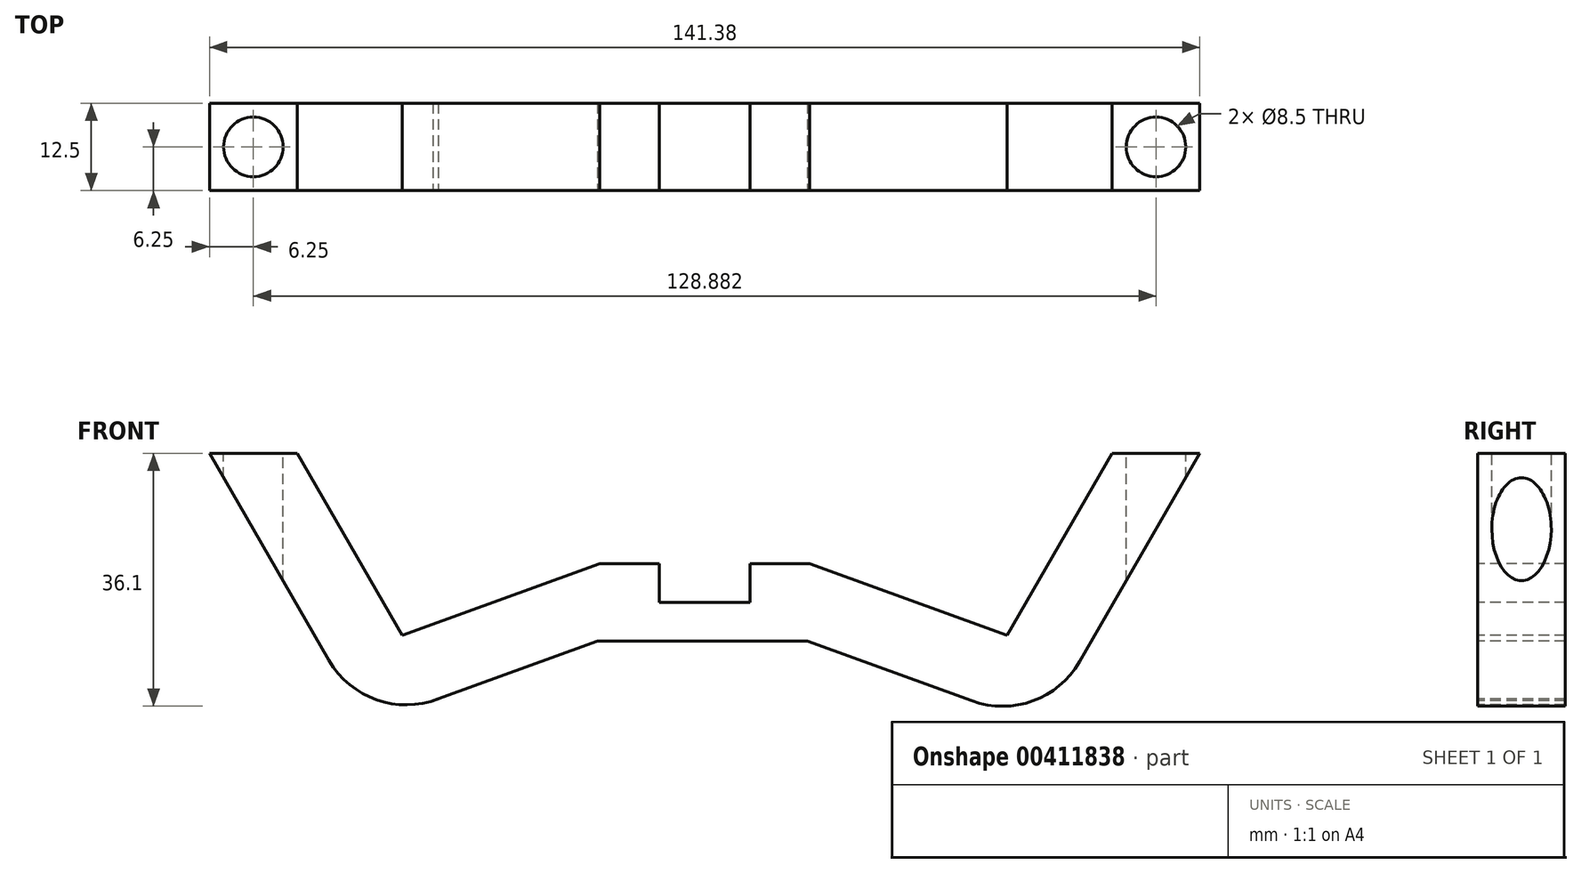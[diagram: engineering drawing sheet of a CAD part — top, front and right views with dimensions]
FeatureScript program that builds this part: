
annotation { "Feature Type Name" : "Feature", "Feature Type Description" : "" }
export const myFeature = defineFeature(function(context is Context, id is Id, definition is map)
    precondition{}
    {
        {
            var Q0;
            Q0=qCreatedBy(makeId("Front.planeOp"),FACE);
            var sketch = newSketch(context, id + "F0", { "sketchPlane" : qUnion([Q0])});
            skLineSegment(sketch, "E0", {"start": v(-35.95, 26.78) * mm, "end": v(-48.45, 26.78) * mm});
            skLineSegment(sketch, "E1", {"start": v(-48.45, 26.78) * mm, "end": v(-63.45, 0.8) * mm});
            skLineSegment(sketch, "E2", {"start": v(-35.95, 26.78) * mm, "end": v(-53.12, -2.97) * mm});
            skLineSegment(sketch, "E3", {"start": v(-63.45, 0.8) * mm, "end": v(-91.64, 11.06) * mm});
            skLineSegment(sketch, "E4", {"start": v(-68.46, -8.55) * mm, "end": v(-91.95, 0) * mm});
            skPoint(sketch, "E5.visualSharp", {"position": v(-58.45, -12.2) * mm});
            skArc(sketch, "E5.filletArc", {"start": v(-68.46, -8.55) * mm, "mid": v(-59.77, -8.55) * mm, "end": v(-53.12, -2.97) * mm});
            skLineSegment(sketch, "E6", {"start": v(-91.64, 11.06) * mm, "end": v(-121.64, 11.06) * mm});
            skLineSegment(sketch, "E7", {"start": v(-91.95, 0) * mm, "end": v(-121.95, 0) * mm});
            skPoint(sketch, "E8", {"position": v(-100.14, 11.06) * mm});
            skPoint(sketch, "E9", {"position": v(-113.14, 11.06) * mm});
            skLineSegment(sketch, "E10", {"start": v(-113.14, 11.06) * mm, "end": v(-113.14, 0) * mm});
            skLineSegment(sketch, "E11", {"start": v(-100.14, 11.06) * mm, "end": v(-100.14, 0) * mm});
            skPoint(sketch, "E12", {"position": v(-113.14, 5.53) * mm});
            skPoint(sketch, "E13", {"position": v(-100.14, 5.53) * mm});
            skLineSegment(sketch, "E14", {"start": v(-113.14, 5.53) * mm, "end": v(-100.14, 5.53) * mm});
            skLineSegment(sketch, "E15", {"start": v(-121.64, 11.06) * mm, "end": v(-149.83, 0.8) * mm});
            skLineSegment(sketch, "E16", {"start": v(-121.95, 0) * mm, "end": v(-145.45, -8.55) * mm});
            skLineSegment(sketch, "E17", {"start": v(-149.83, 0.8) * mm, "end": v(-164.83, 26.78) * mm});
            skLineSegment(sketch, "E18", {"start": v(-164.83, 26.78) * mm, "end": v(-177.33, 26.78) * mm});
            skLineSegment(sketch, "E19", {"start": v(-177.33, 26.78) * mm, "end": v(-160.28, -2.76) * mm});
            skLineSegment(sketch, "E20", {"start": v(-144.68, -8.25) * mm, "end": v(-145.45, -8.55) * mm});
            skPoint(sketch, "E21.visualSharp", {"position": v(-154.83, -12.2) * mm});
            skArc(sketch, "E21.filletArc", {"start": v(-160.28, -2.76) * mm, "mid": v(-153.5, -8.4) * mm, "end": v(-144.68, -8.25) * mm});
            skSolve(sketch);
        }
        {
            var Q0;
            {var subQ1=sQuery(id+"F0.wireOp",EDGE,"E15");Q0=makeQuery(id+"F0.imprint","IMPRINT",FACE,{"disambiguationData":[TD([[makeQuery(id+"F0.imprint","IMPRINT",EDGE,{"derivedFrom":subQ1}),1.0]])]});}
            var Q1;
            {var subQ5=sQuery(id+"F0.wireOp",EDGE,"E14");Q1=makeQuery(id+"F0.imprint","IMPRINT",FACE,{"disambiguationData":[TD([[makeQuery(id+"F0.imprint","IMPRINT",EDGE,{"derivedFrom":subQ5}),1.0]])]});}
            var Q2;
            {var subQ5=sQuery(id+"F0.wireOp",EDGE,"E14");Q2=makeQuery(id+"F0.imprint","IMPRINT",FACE,{"disambiguationData":[TD([[makeQuery(id+"F0.imprint","IMPRINT",EDGE,{"derivedFrom":subQ5}),-1.0]])]});}
            var Q3;
            Q3=makeQuery(id+"F0.imprint","IMPRINT",FACE,{"disambiguationData":[TD([[makeQuery(id+"F0.imprint","IMPRINT",EDGE,{"derivedFrom":sQuery(id+"F0.wireOp",EDGE,"E0")}),1.0]])]});
            extrude(context, id + "F1", {"entities" : qUnion([Q0, Q1, Q2, Q3]), "oppositeDirection" : true, "depth" : 12.5 * mm, "offsetDistance" : 25.4 * mm});
        }
        {
            var Q0;
            Q0=makeQuery(id+"F1.opExtrude","SWEPT_FACE",FACE,{"disambiguationData":[OSD([sQuery(id+"F0.wireOp",EDGE,"E0")])]});
            var sketch = newSketch(context, id + "F2", { "sketchPlane" : qUnion([Q0])});
            skCircle(sketch, "E22", {"center": v(-42.2, 6.25) * mm, "radius": 4.25 * mm});
            skPoint(sketch, "E22.centerSnap0", {"position": v(-42.2, 12.5) * mm});
            skPoint(sketch, "E22.centerSnap1", {"position": v(-35.95, 6.25) * mm});
            skSolve(sketch);
        }
        {
            var Q0;
            Q0=makeQuery(id+"F1.opExtrude","SWEPT_FACE",FACE,{"disambiguationData":[OSD([sQuery(id+"F0.wireOp",EDGE,"E18")])]});
            var sketch = newSketch(context, id + "F3", { "sketchPlane" : qUnion([Q0])});
            skCircle(sketch, "E23", {"center": v(-171.08, 6.25) * mm, "radius": 4.25 * mm});
            skPoint(sketch, "E23.centerSnap0", {"position": v(-171.08, 12.5) * mm});
            skPoint(sketch, "E23.centerSnap1", {"position": v(-177.33, 6.25) * mm});
            skSolve(sketch);
        }
        {
            var Q0;
            Q0=makeQuery(id+"F3.imprint","IMPRINT",FACE,{"disambiguationData":[TD([[makeQuery(id+"F3.imprint","IMPRINT",EDGE,{"derivedFrom":sQuery(id+"F3.wireOp",EDGE,"E23")}),1.0]])]});
            extrude(context, id + "F4", {"entities" : qUnion([Q0]), "operationType" : NewBodyOperationType.REMOVE, "oppositeDirection" : true, "depth" : 33.78 * mm});
        }
        {
            var Q0;
            Q0=makeQuery(id+"F2.imprint","IMPRINT",FACE,{"disambiguationData":[TD([[makeQuery(id+"F2.imprint","IMPRINT",EDGE,{"derivedFrom":sQuery(id+"F2.wireOp",EDGE,"E22")}),1.0]])]});
            extrude(context, id + "F5", {"entities" : qUnion([Q0]), "operationType" : NewBodyOperationType.REMOVE, "oppositeDirection" : true, "depth" : 25.4 * mm});
        }
        {
            var Q0;
            {var subQ5=sQuery(id+"F0.wireOp",EDGE,"E14");Q0=makeQuery(id+"F0.imprint","IMPRINT",FACE,{"disambiguationData":[TD([[makeQuery(id+"F0.imprint","IMPRINT",EDGE,{"derivedFrom":subQ5}),1.0]])]});}
            extrude(context, id + "F6", {"entities" : qUnion([Q0]), "operationType" : NewBodyOperationType.REMOVE, "oppositeDirection" : true, "depth" : 25.4 * mm});
        }
    });
